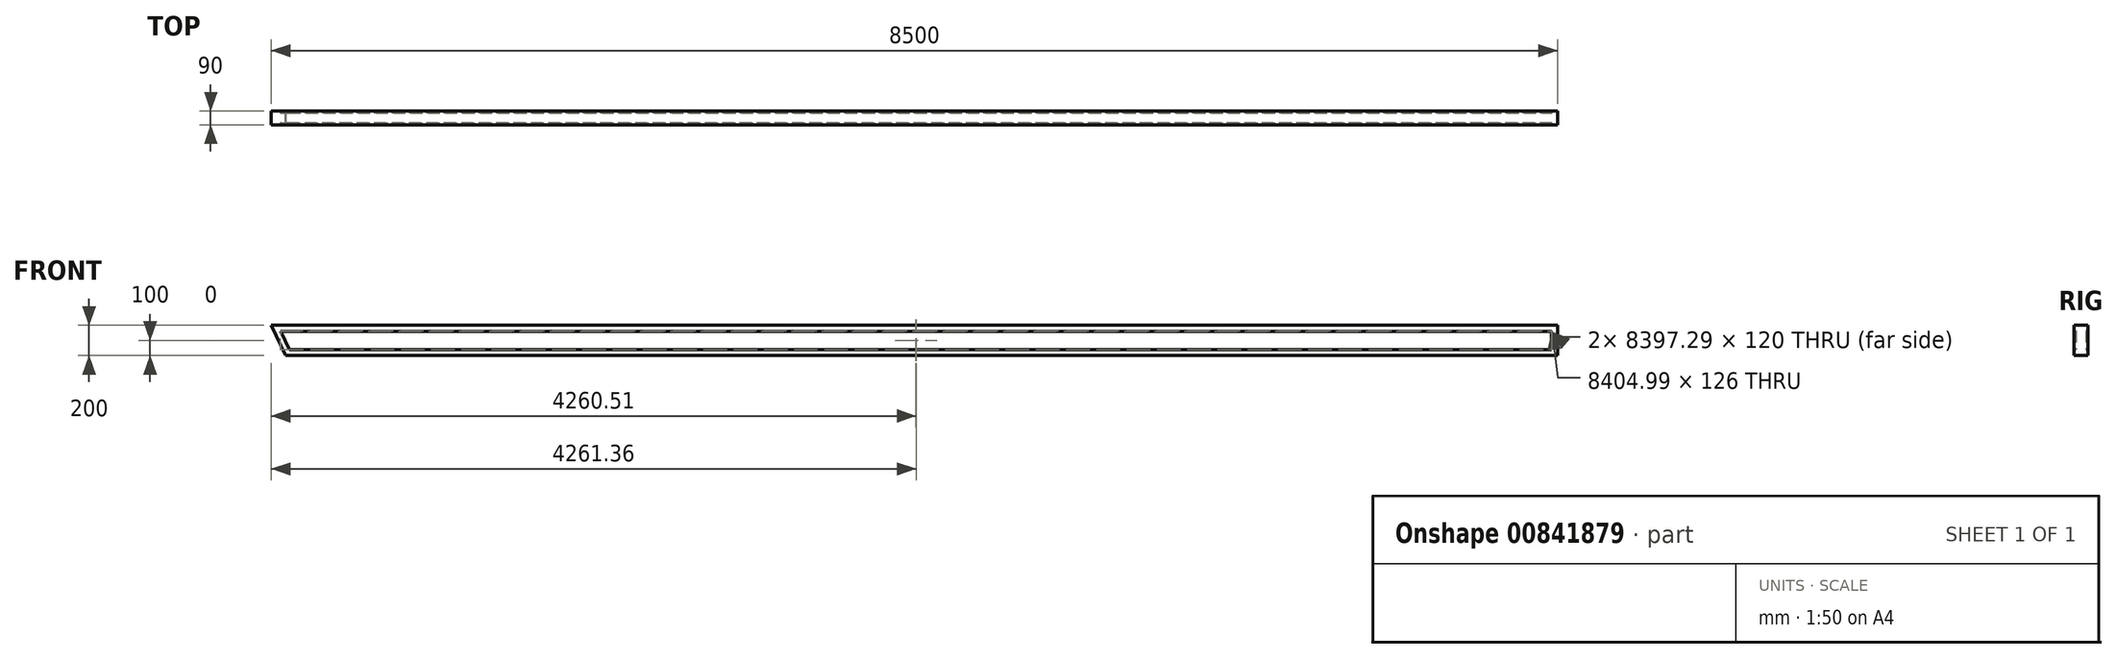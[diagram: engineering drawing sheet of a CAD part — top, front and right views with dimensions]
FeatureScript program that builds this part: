
annotation { "Feature Type Name" : "Feature", "Feature Type Description" : "" }
export const myFeature = defineFeature(function(context is Context, id is Id, definition is map)
    precondition{}
    {
        {
            var Q0;
            Q0=qCreatedBy(makeId("Front.planeOp"),FACE);
            var sketch = newSketch(context, id + "F0", { "sketchPlane" : qUnion([Q0])});
            skLineSegment(sketch, "E0.bottom", {"start": v(0, 0) * mm, "end": v(8407, 0) * mm});
            skLineSegment(sketch, "E0.top", {"start": v(-93, 200) * mm, "end": v(8407, 200) * mm});
            skLineSegment(sketch, "E0.right", {"start": v(8407, 0) * mm, "end": v(8407, 200) * mm});
            skLineSegment(sketch, "E1", {"start": v(-93, 200) * mm, "end": v(0, 0) * mm});
            skPoint(sketch, "E2.orphan", {"position": v(-93, 0) * mm});
            skSolve(sketch);
        }
        {
            var Q0;
            Q0=qCreatedBy(makeId("Right.planeOp"),FACE);
            var sketch = newSketch(context, id + "F1", { "sketchPlane" : qUnion([Q0])});
            skLineSegment(sketch, "E3", {"start": v(0, 0) * mm, "end": v(-45, 0) * mm});
            skLineSegment(sketch, "E4", {"start": v(-45, 0) * mm, "end": v(-45, 40) * mm});
            skLineSegment(sketch, "E5", {"start": v(-45, 40) * mm, "end": v(-33, 40) * mm});
            skLineSegment(sketch, "E6.MirrorCS", {"start": v(45, 40) * mm, "end": v(33, 40) * mm});
            skLineSegment(sketch, "E7.MirrorCS", {"start": v(45, 0) * mm, "end": v(45, 40) * mm});
            skLineSegment(sketch, "E8.MirrorCS", {"start": v(0, 0) * mm, "end": v(45, 0) * mm});
            skLineSegment(sketch, "E9.0", {"start": v(-42, 37) * mm, "end": v(-33, 37) * mm});
            skLineSegment(sketch, "E9.1", {"start": v(-42, 3) * mm, "end": v(-42, 37) * mm});
            skLineSegment(sketch, "E9.2", {"start": v(42, 37) * mm, "end": v(33, 37) * mm});
            skLineSegment(sketch, "E9.3", {"start": v(42, 3) * mm, "end": v(42, 37) * mm});
            skLineSegment(sketch, "E9.4", {"start": v(0, 3) * mm, "end": v(42, 3) * mm});
            skLineSegment(sketch, "E9.5", {"start": v(0, 3) * mm, "end": v(-42, 3) * mm});
            skLineSegment(sketch, "E10", {"start": v(33, 40) * mm, "end": v(33, 37) * mm});
            skLineSegment(sketch, "E11", {"start": v(-33, 40) * mm, "end": v(-33, 37) * mm});
            skSolve(sketch);
        }
        {
            var Q0;
            Q0 = qSketchRegion(id + "F1", true);
            var Q1;
            Q1 = qConstructionFilter(qBodyType(qCreatedBy(id + "F0" ,EDGE), BodyType.WIRE), ConstructionObject.NO);
            sweep(context, id + "F2", {"profiles" : qUnion([Q0]), "path" : qUnion([Q1])});
        }
    });
